# Revit family: Shower-Handshower_Kit-KOHLER-AVID-K-97368T_1
name_source: partatom
category: Plumbing Fixtures
units: mm (PartAtom-declared; Revit-internal decimal feet)

## family parameters
Cut with Voids When Loaded = No
Host = Face
OmniClass Number = 23.31.17.00
OmniClass Title = Showers
Part Type = Normal
Room Calculation Point = No
Round Connector Dimension = Use Diameter
Shared = No

## types (4) — shared parameters
ADA Compliant = No
Assembly Code = D2010700
CW Connection = Yes
Cold Water Inlet = Cold Water Inlet
Date Modified = 03/12/2023
Default Elevation = 42"
Drain Included = No
Flow Rate = 2 GPM
HW Connection = Yes
Handle Clearance = 2 9/16"
Height = 20 11/16"
Hot Water Inlet = Hot Water Inlet
Length = 4 5/8"
Manufacturer = Kohler Co.
Master Format 2014 = 22 42 23
Master Format 2014 Name = Residential Showers
Material = Premium Metal Construction
Pressure = 45.00 psi
Product Name = AVID
URL = http://www.kohler.com.cn
Vent Connection = No
Waste Connection = No
Waste Water Outlet = Waste Water Outlet
WaterSense Certified = No
Width = 19 5/16"

## per-type parameters (varying)
| type | Description | Finish | Model | Product Page URL | Type |
| 1.8 GPM, CP-Polished Chrome | Wall-Mounted Shower Faucet | Kohler-Metal-CP-Polished_Chrome | K-97368T-4-CP | https://www.kohler.com.cn | 1 |
| 1.8 GPM, TT-Titanium Silver | Wall-Mounted Shower Faucet | Kohler-Metal-TT-Titanium_Silver | K-97368T-4-TT | https://www.kohler.com.cn | 2 |
| 1.849 GPM, CP-Polished Chrome | Exposed Wall Mount Shower Only Faucet | Kohler-Metal-CP-Polished_Chrome | K-97368T-4E2-CP |  | 3 |
| 1.849 GPM, TT-Titanium Silver | Exposed Wall Mount Shower Only Faucet | Kohler-Metal-TT-Titanium_Silver | K-97368T-4E2-TT |  | 4 |

## geometry (parser evidence)
native form markers: Sweep x5
no freeform markers — native parametric forms only
